# Revit family: BDG_BossDesign_Tbls_Reef_Poser1
name_source: partatom
category: Furniture
revit_build: Autodesk Revit 2016 (Build: 20150220_1215(x64)
units: mm (PartAtom-declared; Revit-internal decimal feet)

## family parameters
Always vertical = Yes
Cut with Voids When Loaded = No
OmniClass Number = 23.40.20.00
OmniClass Title = General Furniture and Specialties
Room Calculation Point = No
Shared = Yes
Work Plane-Based = No

## types (14) — shared parameters
Assembly Code = E2020200
AssetType = Movable
Category = Pr_40_50_21 : Desks, tables and worktops
DurationUnit = year
ExpectedLife = 5
IfcExportAs = IfcFurnishingElementType
IfcExportType = TABLE
Keynote = Pr_40_50_21
ManufacturerName = Boss Design
ManufacturerURL = www.bossdesign.com
NBSDescription = Tables
NBSReference = 45-35-86/327
Name = Tables_Reef_Poseur_BossDesign
NominalHeight = 1100 mm
ProductInformation = www.bossdesign.com/product-list/reef
URL = www.bossdesign.com
Uniclass2015Code = Pr_40_50_21
Uniclass2015Title = Desks, tables and worktops
Uniclass2015Version = Products v1.10
Version = 1
WarrantyDescription = Structural Warranty Excludes Foams and Fabrics
WarrantyDurationLabor = 5
WarrantyDurationParts = 5
WarrantyDurationUnit = year
zero-valued in all types: NumberOfChairs, UndersideSupportOffset, WorksurfaceArea

## per-type parameters (varying)
| type | BIMObjectName | CircularBase | CircularTop | Description | Gap | Is2ndBase | LeftBaseOffsetforRectangleTop | LengthBetweenFeet | Model | ModelNumber | ModelReference | NominalLength | NominalLengthBaseCircle | NominalLengthBaseSquare | NominalWidth | RightBaseOffsetforRectangleTop | Shape | Size | SquareBase | SquareTop |
| 600mm x 600mm MFC top, 500mm x 500mm base, poseur | BDG_BossDesign_Tables_Reef_Poseur | No | No | 600mm x 600mm MFC top, grey, black or white 500mm x 500mm base, poseur | 100 mm  [stored 0.328084 ft] | No | 200 mm  [stored 0.656168 ft] | 400 mm  [stored 1.31234 ft] | RF600SS P | RF600SS P | 600mm x 600mm MFC top, grey, black or white 500mm x 500mm base, poseur | 600 mm | 500 mm  [stored 1.64042 ft] | 500 mm  [stored 1.64042 ft] | 600 mm | 200 mm  [stored 0.656168 ft] | Square | 600 x 600 x 1100mm | Yes | Yes |
| 600mm dia MFC top, 600mm dia base, poseur | BDG_BossDesign_Tables_Reef_Poseur | Yes | Yes | 600mm dia MFC top, grey, black or white 600mm dia base, poseur | 100 mm  [stored 0.328084 ft] | No | 250 mm  [stored 0.82021 ft] | 500 mm  [stored 1.64042 ft] | RF600CC P | RF600CC P | 600mm dia MFC top, grey, black or white 600mm dia base, poseur | 600 mm | 600 mm | 600 mm | 600 mm | 250 mm  [stored 0.82021 ft] | Circular | 600 ø x 1100mm | No | No |
| 1200mm x 800mm MFC top, 500mm x 500mm base, poseur | BDG_BossDesign_Tables_Reef_Poseur | No | No | 1200mm x 800mm MFC top, grey, black or white 500mm x 500mm base, poseur | 100 mm  [stored 0.328084 ft] | Yes | 500 mm  [stored 1.64042 ft] | 400 mm  [stored 1.31234 ft] | RF1280 CSR P | RF1280 CSR P | 1200mm x 800mm MFC top, grey, black or white 500mm x 500mm base, poseur | 1200 mm | 500 mm  [stored 1.64042 ft] | 500 mm  [stored 1.64042 ft] | 800 mm  [stored 2.62467 ft] | 500 mm  [stored 1.64042 ft] | Rectangular | 1200 x 800 x 1100mm | Yes | Yes |
| 1200mm x 600mm MFC top, 500mm x 500mm base, poseur | BDG_BossDesign_Tables_Reef_Poseur | No | No | 1200mm x 600mm MFC top, grey, black or white 500mm x 500mm base, poseur | 100 mm  [stored 0.328084 ft] | Yes | 500 mm  [stored 1.64042 ft] | 400 mm  [stored 1.31234 ft] | RF1200 CSR P | RF1200 CSR P | 1200mm x 600mm MFC top, grey, black or white 500mm x 500mm base, poseur | 1200 mm | 500 mm  [stored 1.64042 ft] | 500 mm  [stored 1.64042 ft] | 600 mm | 500 mm  [stored 1.64042 ft] | Rectangular | 1200 x 600 x 1100mm | Yes | Yes |
| 1400mm x 700mm MFC top, 500mm x 500mm base, poseur | BDG_BossDesign_Tables_Reef_Poseur

BDG_BossDesign_Tables_Reef_Poseur | No | No | 1400mm x 700mm MFC top, grey, black or white 500mm x 500mm base, poseur | 250 mm  [stored 0.82021 ft] | Yes | 500 mm  [stored 1.64042 ft] | 400 mm  [stored 1.31234 ft] | RF1470 CSR P | RF1470 CSR P | 1400mm x 700mm MFC top, grey, black or white 500mm x 500mm base, poseur | 1400 mm  [stored 4.59318 ft] | 500 mm  [stored 1.64042 ft] | 500 mm  [stored 1.64042 ft] | 700 mm  [stored 2.29659 ft] | 500 mm  [stored 1.64042 ft] | Rectangular | 1400 x 700 x 1100mm | Yes | Yes |
| 1400mm x 700mm MFC top, 600mm dia base, poseur | BDG_BossDesign_Tables_Reef_Poseur | Yes | No | 1400mm x 700mm MFC top, grey, black or white 600mm dia base, poseur | 150 mm | Yes | 600 mm | 500 mm  [stored 1.64042 ft] | RF1470 CCR P | RF1470 CCR P | 1400mm x 700mm MFC top, grey, black or white 600mm dia base, poseur | 1400 mm  [stored 4.59318 ft] | 600 mm | 600 mm | 700 mm  [stored 2.29659 ft] | 600 mm | Rectangular | 1400 x 700 x 1100mm | No | Yes |
| 1600mm x 800mm MFC top, 500mm x 500mm base, poseur | BDG_BossDesign_Tables_Reef_Poseur | No | No | 1600mm x 800mm MFC top, grey, black or white 500mm x 500mm base, poseur | 300 mm  [stored 0.984252 ft] | Yes | 500 mm  [stored 1.64042 ft] | 400 mm  [stored 1.31234 ft] | RF1680 CSR P | RF1680 CSR P | 1600mm x 800mm MFC top, grey, black or white 500mm x 500mm base, poseur | 1600 mm  [stored 5.24934 ft] | 500 mm  [stored 1.64042 ft] | 500 mm  [stored 1.64042 ft] | 800 mm  [stored 2.62467 ft] | 500 mm  [stored 1.64042 ft] | Rectangular | 1600 x 800 x 1100mm | Yes | Yes |
| 1600mm x 800mm MFC top, 600mm dia base, poseur | BDG_BossDesign_Tables_Reef_Poseur | Yes | No | 1600mm x 800mm MFC top, grey, black or white 600mm dia base, poseur | 200 mm  [stored 0.656168 ft] | Yes | 600 mm | 500 mm  [stored 1.64042 ft] | RF1680 CCR P | RF1680 CCR P | 1600mm x 800mm MFC top, grey, black or white 600mm dia base, poseur | 1600 mm  [stored 5.24934 ft] | 600 mm | 600 mm | 800 mm  [stored 2.62467 ft] | 600 mm | Rectangular | 1600 x 800 x 1100mm | No | Yes |
| 600mm x 600mm MFC top, 600mm dia base, poseur | BDG_BossDesign_Tables_Reef_Poseur | Yes | No | 600mm x 600mm MFC top, grey, black or white 600mm dia base, poseur | 100 mm  [stored 0.328084 ft] | No | 250 mm  [stored 0.82021 ft] | 500 mm  [stored 1.64042 ft] | RF600SC P | RF600SC P | 600mm x 600mm MFC top, grey, black or white 600mm dia base, poseur | 600 mm | 600 mm | 600 mm | 600 mm | 250 mm  [stored 0.82021 ft] | Square | 600 x 600 x 1100mm | No | Yes |
| 600mm dia MFC top, 500mm x 500mm base, poseur | BDG_BossDesign_Tables_Reef_Poseur | No | Yes | 600mm dia MFC top, grey, black or white 500mm x 500mm base, poseur | 100 mm  [stored 0.328084 ft] | No | 200 mm  [stored 0.656168 ft] | 400 mm  [stored 1.31234 ft] | RF600CS P | RF600CS P | 600mm dia MFC top, grey, black or white 500mm x 500mm base, poseur | 600 mm | 500 mm  [stored 1.64042 ft] | 500 mm  [stored 1.64042 ft] | 600 mm | 200 mm  [stored 0.656168 ft] | Circular | 600 ø x 1100mm | Yes | No |
| 800mm x 800mm MFC top, 600mm dia base, poseur | BDG_BossDesign_Tables_Reef_Poseur | Yes | No | 800mm x 800mm MFC top, grey, black or white 600mm dia base, poseur | 100 mm  [stored 0.328084 ft] | No | 250 mm  [stored 0.82021 ft] | 500 mm  [stored 1.64042 ft] | RF800SC P | RF800SC P | 800mm x 800mm MFC top, grey, black or white 600mm dia base, poseur | 800 mm  [stored 2.62467 ft] | 600 mm | 600 mm | 800 mm  [stored 2.62467 ft] | 250 mm  [stored 0.82021 ft] | Square | 800 x 800 x 1100mm | No | Yes |
| 800mm dia MFC top, 600mm dia base, poseur | BDG_BossDesign_Tables_Reef_Poseur | Yes | Yes | 800mm dia MFC top, grey, black or white 600mm dia base, poseur | 100 mm  [stored 0.328084 ft] | No | 250 mm  [stored 0.82021 ft] | 500 mm  [stored 1.64042 ft] | RF800CC P | RF800CC P | 800mm dia MFC top, grey, black or white 600mm dia base, poseur | 800 mm  [stored 2.62467 ft] | 600 mm | 600 mm | 800 mm  [stored 2.62467 ft] | 250 mm  [stored 0.82021 ft] | Circular | 800 ø x 1100mm | No | No |
| 800mm x 800mm MFC top, 500mm x 500mm base, poseur | BDG_BossDesign_Tables_Reef_Poseur | No | No | 800mm x 800mm MFC top, grey, black or white 500mm x 500mm base, poseur | 100 mm  [stored 0.328084 ft] | No | 200 mm  [stored 0.656168 ft] | 400 mm  [stored 1.31234 ft] | RF800SS P | RF800SS P | 800mm x 800mm MFC top, grey, black or white 500mm x 500mm base, poseur | 800 mm  [stored 2.62467 ft] | 500 mm  [stored 1.64042 ft] | 500 mm  [stored 1.64042 ft] | 800 mm  [stored 2.62467 ft] | 200 mm  [stored 0.656168 ft] | Square | 800 x 800 x 1100mm | Yes | Yes |
| 800mm dia MFC top, 500mm x 500mm base, poseur | BDG_BossDesign_Tables_Reef_Poseur | No | Yes | 800mm dia MFC top, grey, black or white 500mm x 500mm base, poseur | 100 mm  [stored 0.328084 ft] | No | 200 mm  [stored 0.656168 ft] | 400 mm  [stored 1.31234 ft] | RF800CS P | RF800CS P | 800mm dia MFC top, grey, black or white 500mm x 500mm base, poseur | 800 mm  [stored 2.62467 ft] | 500 mm  [stored 1.64042 ft] | 500 mm  [stored 1.64042 ft] | 800 mm  [stored 2.62467 ft] | 200 mm  [stored 0.656168 ft] | Circular | 800 ø x 1100mm | Yes | No |

note: [stored X ft] marks values corroborated as IEEE doubles in the binary element streams (Revit-internal decimal feet)

## geometry (parser evidence)
native form markers: Sweep x1
no freeform markers — native parametric forms only
